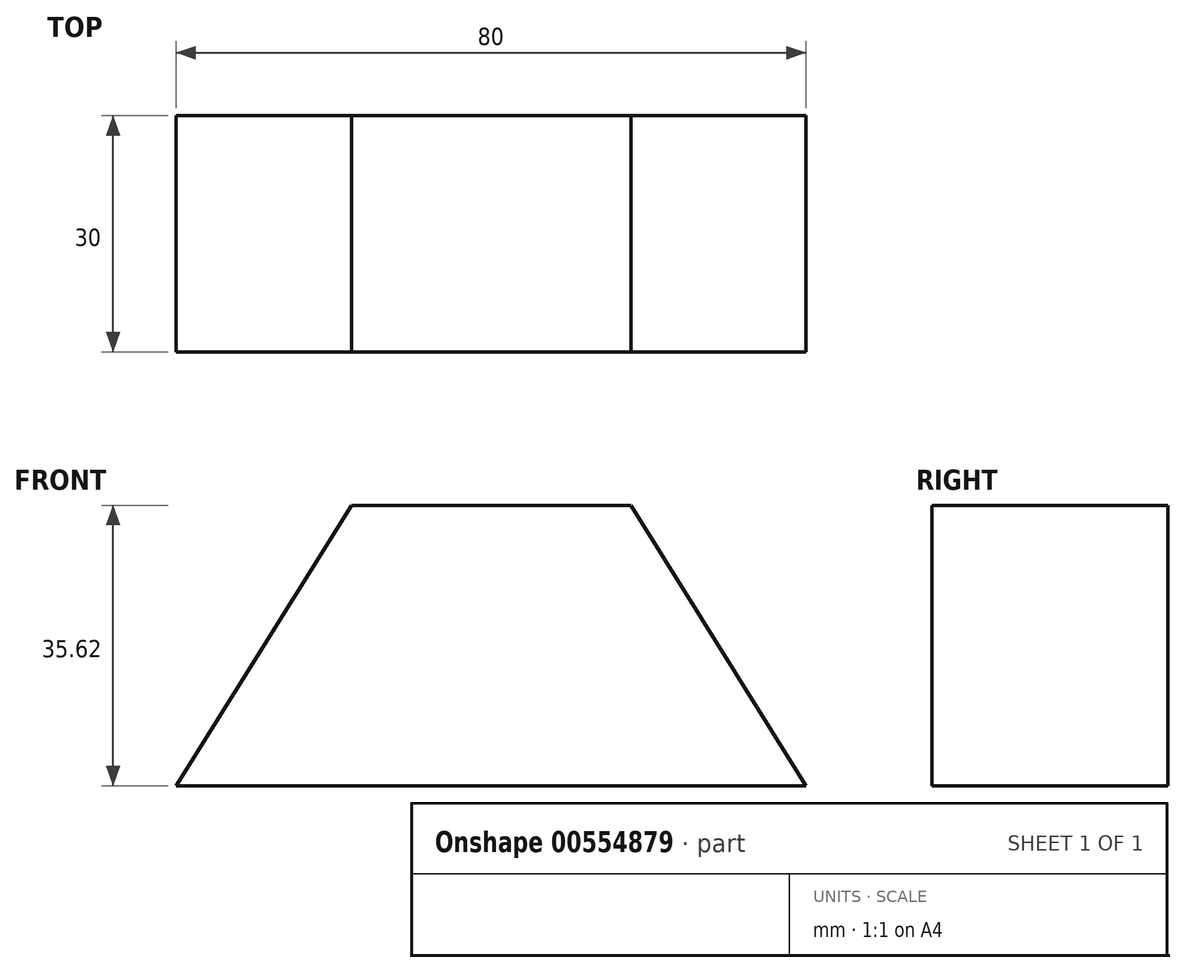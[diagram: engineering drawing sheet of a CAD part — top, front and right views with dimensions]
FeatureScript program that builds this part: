
annotation { "Feature Type Name" : "Feature", "Feature Type Description" : "" }
export const myFeature = defineFeature(function(context is Context, id is Id, definition is map)
    precondition{}
    {
        {
            var Q0;
            Q0=qCreatedBy(makeId("Front.planeOp"),FACE);
            var sketch = newSketch(context, id + "F0", { "sketchPlane" : qUnion([Q0])});
            skLineSegment(sketch, "E0", {"start": v(-41.16, -41.18) * mm, "end": v(38.84, -41.18) * mm});
            skLineSegment(sketch, "E1", {"start": v(-41.16, -41.18) * mm, "end": v(-18.9, -5.56) * mm});
            skLineSegment(sketch, "E2", {"start": v(38.84, -41.18) * mm, "end": v(16.59, -5.56) * mm});
            skLineSegment(sketch, "E3", {"start": v(-18.9, -5.56) * mm, "end": v(16.59, -5.56) * mm});
            skSolve(sketch);
        }
        {
            var Q0;
            Q0 = qSketchRegion(id + "F0", true);
            extrude(context, id + "F1", {"entities" : qUnion([Q0]), "depth" : 30 * mm, "offsetDistance" : 25 * mm});
        }
    });
